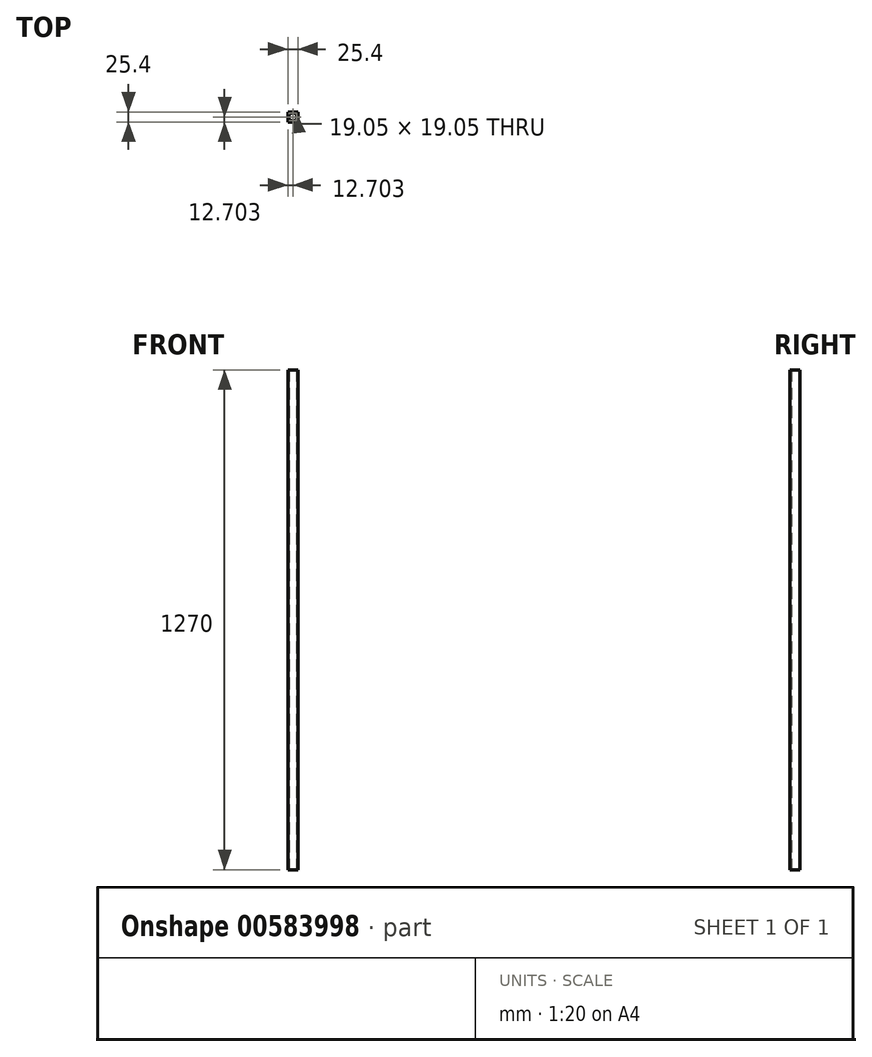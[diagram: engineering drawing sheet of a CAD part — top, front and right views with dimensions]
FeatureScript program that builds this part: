
annotation { "Feature Type Name" : "Feature", "Feature Type Description" : "" }
export const myFeature = defineFeature(function(context is Context, id is Id, definition is map)
    precondition{}
    {
        {
            var Q0;
            Q0=qCreatedBy(makeId("Top.planeOp"),FACE);
            var sketch = newSketch(context, id + "F0", { "sketchPlane" : qUnion([Q0])});
            skLineSegment(sketch, "E0.bottom", {"start": v(-6.57, 8.24) * mm, "end": v(12.48, 8.24) * mm});
            skLineSegment(sketch, "E0.top", {"start": v(-6.57, -10.81) * mm, "end": v(12.48, -10.81) * mm});
            skLineSegment(sketch, "E0.left", {"start": v(-6.57, 8.24) * mm, "end": v(-6.57, -10.81) * mm});
            skLineSegment(sketch, "E0.right", {"start": v(12.48, 8.24) * mm, "end": v(12.48, -10.81) * mm});
            skLineSegment(sketch, "E1.bottom", {"start": v(-9.75, 11.41) * mm, "end": v(15.65, 11.41) * mm});
            skLineSegment(sketch, "E1.top", {"start": v(-9.75, -13.99) * mm, "end": v(15.65, -13.99) * mm});
            skLineSegment(sketch, "E1.left", {"start": v(-9.75, 11.41) * mm, "end": v(-9.75, -13.99) * mm});
            skLineSegment(sketch, "E1.right", {"start": v(15.65, 11.41) * mm, "end": v(15.65, -13.99) * mm});
            skSolve(sketch);
        }
        {
            var Q0;
            Q0=makeQuery(id+"F0.imprint","IMPRINT",FACE,{"disambiguationData":[TD([[makeQuery(id+"F0.imprint","IMPRINT",EDGE,{"derivedFrom":sQuery(id+"F0.wireOp",EDGE,"E0.bottom")}),1.0]])]});
            extrude(context, id + "F1", {"entities" : qUnion([Q0]), "depth" : 1270 * mm, "offsetDistance" : 25.4 * mm});
        }
    });
